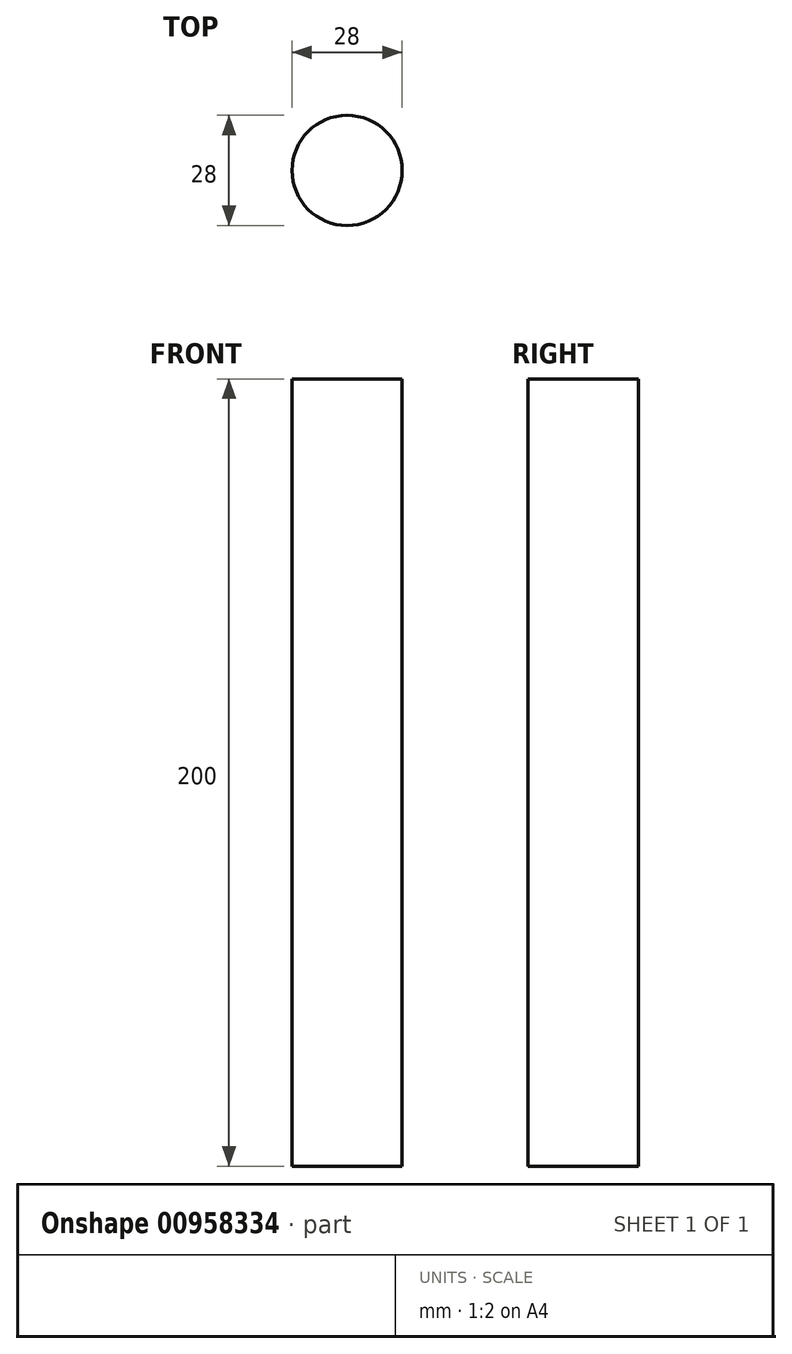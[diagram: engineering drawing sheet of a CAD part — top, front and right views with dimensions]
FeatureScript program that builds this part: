
annotation { "Feature Type Name" : "Feature", "Feature Type Description" : "" }
export const myFeature = defineFeature(function(context is Context, id is Id, definition is map)
    precondition{}
    {
        {
            var Q0;
            Q0=qCreatedBy(makeId("Top.planeOp"),FACE);
            var sketch = newSketch(context, id + "F0", { "sketchPlane" : qUnion([Q0])});
            skCircle(sketch, "E0", {"center": v(0, 0) * mm, "radius": 14 * mm});
            skSolve(sketch);
        }
        {
            var Q0;
            Q0=makeQuery(id+"F0.imprint","IMPRINT",FACE,{"disambiguationData":[TD([[makeQuery(id+"F0.imprint","IMPRINT",EDGE,{"derivedFrom":sQuery(id+"F0.wireOp",EDGE,"E0")}),1.0]])]});
            extrude(context, id + "F1", {"entities" : qUnion([Q0]), "depth" : 200 * mm, "offsetDistance" : 25 * mm});
        }
    });
